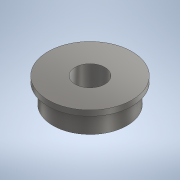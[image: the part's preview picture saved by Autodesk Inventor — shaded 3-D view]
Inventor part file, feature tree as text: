
AUTODESK INVENTOR PART (.ipt)
format: ipt  version: 2020 (Build 240168000, 168)  size: 124,416 bytes
history: native  units: mm
features: extrude x2, sketch x2, other x1
ambient origin geometry x8: Origin, YZ Plane, XZ Plane, XY Plane, X Axis, Y Axis, Z Axis, Center Point
bodies: Body1 (feature_tree)
feature tree (5):
  other  "ソリッド1"
  extrude  "押し出し1"  Depth=6.0mm
  extrude  "押し出し2"  Depth=15.0mm
  sketch  "スケッチ1"
  sketch  "スケッチ2"
